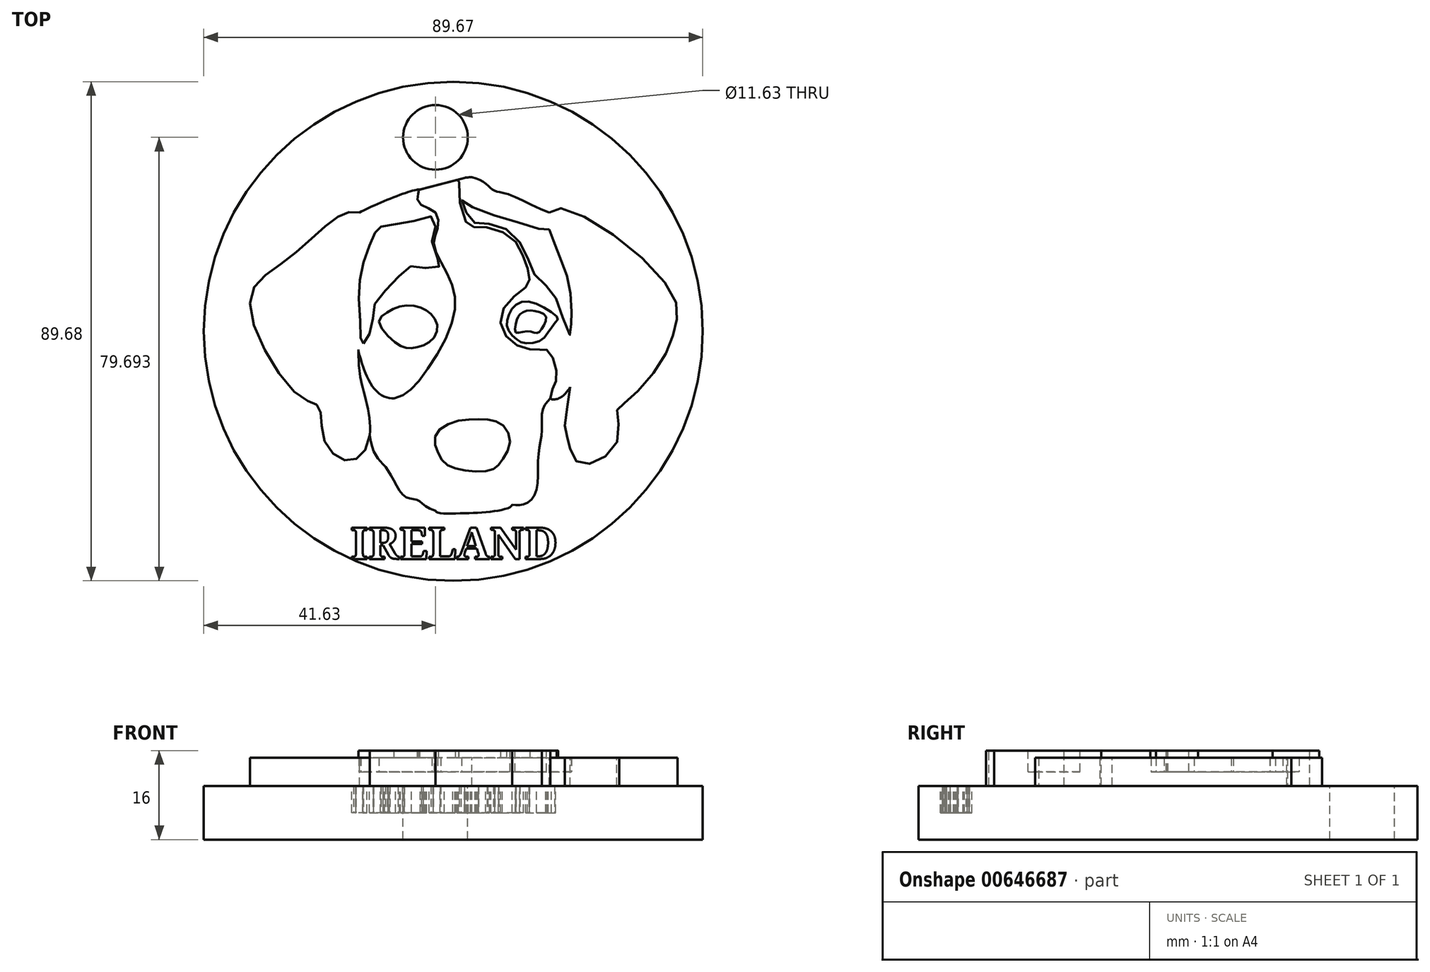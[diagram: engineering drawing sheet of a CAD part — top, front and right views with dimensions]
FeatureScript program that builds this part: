
annotation { "Feature Type Name" : "Feature", "Feature Type Description" : "" }
export const myFeature = defineFeature(function(context is Context, id is Id, definition is map)
    precondition{}
    {
        {
            var Q0;
            Q0=qCreatedBy(makeId("Top.planeOp"),FACE);
            var sketch = newSketch(context, id + "F0", { "sketchPlane" : qUnion([Q0])});
            skFitSpline(sketch, "E0", {"points": [v(-13.66, 27.6) * mm, v(-17.78, 26.67) * mm, v(-26.99, 18.92) * mm, v(-33.34, 11.59) * mm, v(-24.19, -5.58) * mm, v(-20.88, -7.44) * mm, v(-19.85, -13.65) * mm, v(-15.1, -16.96) * mm, v(-11.8, -12.41) * mm, v(-13.44, -2.27) * mm, v(-13.85, 2.98) * mm, v(-13.45, 18.91) * mm, v(-11.04, 25.53) * mm, v(-13.66, 27.6) * mm]});
            skFitSpline(sketch, "E1", {"points": [v(0, -25.98) * mm, v(3.57, -26.47) * mm, v(11.16, -25.98) * mm, v(13.75, -24.88) * mm, v(10.75, -22.95) * mm, v(6.62, -21.3) * mm, v(3.93, -22.74) * mm, v(0, -25.98) * mm]});
            skFitSpline(sketch, "E2", {"points": [v(23.24, -10.9) * mm, v(24.17, -3.78) * mm, v(23.78, 0) * mm, v(25.02, 13.65) * mm, v(20.47, 27.6) * mm, v(26.06, 27.2) * mm, v(42.53, 13.13) * mm, v(43.15, 7.35) * mm, v(40.44, 0.6) * mm, v(34.11, -6.54) * mm, v(32.64, -7.95) * mm, v(32.88, -12.87) * mm, v(28.45, -17.37) * mm, v(25.02, -16.8) * mm, v(23.78, -13.02) * mm, v(23.24, -10.9) * mm]});
            skFitSpline(sketch, "E3", {"points": [v(-13.66, 27.6) * mm, v(-2.96, 31.69) * mm, v(-3.17, 30.85) * mm, v(-2.86, 29.23) * mm, v(0, 27.6) * mm, v(0.34, 24.56) * mm, v(-0.27, 21.79) * mm, v(2.5, 15.8) * mm, v(3.07, 8.14) * mm, v(-3.5, -3.23) * mm, v(-7.45, -5.77) * mm], "startDerivative": vector(49.88, 27.02) * mm, "endDerivative": vector(-51.5, -11.1) * mm});
            skFitSpline(sketch, "E4", {"points": [v(-7.45, -5.77) * mm, v(-10.9, -4.19) * mm, v(-13.44, 1.24) * mm, v(-13.85, 2.98) * mm], "startDerivative": vector(-9.26, -1.19) * mm, "endDerivative": vector(-0.89, 6.86) * mm});
            skFitSpline(sketch, "E5", {"points": [v(6.53, 33.93) * mm, v(4.34, 33.05) * mm, v(5.76, 25.5) * mm, v(7.62, 25.06) * mm, v(13.32, 23.41) * mm, v(16.05, 19.03) * mm, v(16.93, 15.64) * mm, v(16.08, 14.05) * mm, v(12.22, 10.38) * mm, v(12.4, 5.78) * mm, v(16.08, 3.19) * mm, v(18.66, 2.98) * mm, v(19.89, 2.98) * mm, v(21.2, 1.24) * mm, v(21.75, -2.27) * mm, v(21.2, -3.75) * mm, v(20.65, -5.77) * mm, v(22.19, -5.77) * mm, v(24.17, -3.78) * mm], "startDerivative": vector(-56.64, 0.9) * mm, "endDerivative": vector(31.08, 53.1) * mm});
            skFitSpline(sketch, "E6", {"points": [v(6.53, 33.93) * mm, v(10.37, 31.69) * mm, v(13.2, 30.85) * mm, v(20.47, 27.6) * mm], "startDerivative": vector(20.86, -3.29) * mm, "endDerivative": vector(18.77, -6.28) * mm});
            skLineSegment(sketch, "E7", {"start": v(-2.96, 31.69) * mm, "end": v(5.26, 33.84) * mm});
            skFitSpline(sketch, "E8", {"points": [v(0, -25.98) * mm, v(-3.11, -24.12) * mm, v(-5.41, -23.46) * mm, v(-8.37, -18.97) * mm, v(-10.34, -16.56) * mm, v(-11.8, -12.41) * mm], "startDerivative": vector(-27.57, 6.34) * mm, "endDerivative": vector(-3.27, 28.64) * mm});
            skFitSpline(sketch, "E9", {"points": [v(13.75, -24.88) * mm, v(15.73, -24.88) * mm, v(17.92, -22.95) * mm, v(18.46, -16.45) * mm, v(19.12, -11.63) * mm, v(19.23, -8.02) * mm, v(20.65, -5.77) * mm], "startDerivative": vector(15.52, -2.17) * mm, "endDerivative": vector(13.18, 11.7) * mm});
            skFitSpline(sketch, "E10", {"points": [v(2.15, -17.77) * mm, v(0.52, -15.73) * mm, v(0, -12.4) * mm, v(3.62, -9.95) * mm, v(8.39, -9.56) * mm, v(11.64, -10.26) * mm, v(13.43, -13.39) * mm, v(11.9, -17) * mm, v(10.36, -18.53) * mm, v(6.3, -18.86) * mm, v(2.15, -17.77) * mm]});
            skFitSpline(sketch, "E11", {"points": [v(-8.57, 8.24) * mm, v(-7.53, 9.28) * mm, v(-5.74, 9.76) * mm, v(-4.01, 9.42) * mm, v(-2.9, 8.1) * mm, v(-2.84, 6.1) * mm, v(-4.01, 5.55) * mm, v(-6.08, 5.62) * mm, v(-7.8, 7.14) * mm, v(-8.57, 8.24) * mm]});
            skFitSpline(sketch, "E12", {"points": [v(14.44, 6.05) * mm, v(15.87, 6.21) * mm, v(17.51, 6.1) * mm, v(18.4, 6) * mm, v(19.16, 6.81) * mm, v(19.89, 8.84) * mm, v(18.4, 9.77) * mm, v(16.36, 9.94) * mm, v(15.05, 9.17) * mm, v(14.55, 7.96) * mm, v(14.44, 6.05) * mm]});
            skFitSpline(sketch, "E13", {"points": [v(-10.13, 8) * mm, v(-8.57, 9.74) * mm, v(-5.74, 10.87) * mm, v(-2.65, 10.52) * mm, v(-0.74, 9.28) * mm, v(0.36, 7.1) * mm, v(-0.75, 4.59) * mm, v(-3.14, 3.45) * mm, v(-5.08, 3.25) * mm, v(-7.25, 4.3) * mm, v(-10.13, 8) * mm]});
            skFitSpline(sketch, "E14", {"points": [v(12.9, 8.26) * mm, v(13.84, 10.38) * mm, v(15.89, 11.62) * mm, v(19.75, 10.38) * mm, v(22, 8.58) * mm, v(21.8, 8.13) * mm, v(20.4, 6.28) * mm, v(18.89, 4.6) * mm, v(16.14, 4.1) * mm, v(14.57, 4.8) * mm, v(13.1, 6.53) * mm, v(12.9, 8.26) * mm]});
            skFitSpline(sketch, "E15", {"points": [v(-12.92, 4.07) * mm, v(-12, 5.37) * mm, v(-11.2, 8.75) * mm, v(-10.7, 11.58) * mm, v(-7.39, 15.2) * mm, v(-4.56, 17.91) * mm, v(-1.6, 17.6) * mm, v(0.8, 17.98) * mm, v(0.93, 18.31) * mm, v(-0.57, 21.79) * mm, v(0, 24.99) * mm, v(-0.57, 26.82) * mm, v(-4.74, 25.84) * mm, v(-8.78, 25.33) * mm, v(-10.6, 24.56) * mm, v(-10.86, 23.85) * mm, v(-12.26, 20.72) * mm, v(-13.43, 16.42) * mm, v(-13.73, 11.59) * mm, v(-13.43, 5.63) * mm, v(-13.43, 4.37) * mm, v(-12.92, 4.07) * mm]});
            skFitSpline(sketch, "E16", {"points": [v(5.52, 27.6) * mm, v(4.74, 29.78) * mm, v(6.5, 28.65) * mm, v(13.77, 26.16) * mm, v(19.38, 24.56) * mm, v(20.4, 24.56) * mm, v(20.95, 23.33) * mm, v(23, 17.96) * mm, v(23.92, 15.13) * mm, v(24.46, 10.05) * mm, v(24.36, 8.25) * mm, v(24.27, 5.56) * mm, v(22.66, 9.42) * mm, v(20.85, 13.52) * mm, v(18.07, 16.1) * mm, v(16.75, 19.04) * mm, v(14.2, 23.43) * mm, v(10.06, 25.53) * mm, v(7.08, 25.72) * mm, v(5.52, 27.6) * mm]});
            skSolve(sketch);
        }
        {
            var Q0;
            Q0=qSketchRegion(id+"F0",true);
            var Q1;
            Q1=makeQuery(id+"F0.imprint","IMPRINT",FACE,{"disambiguationData":[TD([[makeQuery(id+"F0.imprint","IMPRINT",EDGE,{"derivedFrom":sQuery(id+"F0.wireOp",EDGE,"E11")}),1.0]])]});
            var Q2;
            Q2=makeQuery(id+"F0.imprint","IMPRINT",FACE,{"disambiguationData":[TD([[makeQuery(id+"F0.imprint","IMPRINT",EDGE,{"derivedFrom":sQuery(id+"F0.wireOp",EDGE,"E15")}),1.0]])]});
            var Q3;
            Q3=makeQuery(id+"F0.imprint","IMPRINT",FACE,{"disambiguationData":[TD([[makeQuery(id+"F0.imprint","IMPRINT",EDGE,{"derivedFrom":sQuery(id+"F0.wireOp",EDGE,"E12")}),1.0]])]});
            var Q4;
            Q4=makeQuery(id+"F0.imprint","IMPRINT",FACE,{"disambiguationData":[TD([[makeQuery(id+"F0.imprint","IMPRINT",EDGE,{"derivedFrom":sQuery(id+"F0.wireOp",EDGE,"E12")}),-1.0]])]});
            var Q5;
            Q5=makeQuery(id+"F0.imprint","IMPRINT",FACE,{"disambiguationData":[TD([[makeQuery(id+"F0.imprint","IMPRINT",EDGE,{"derivedFrom":sQuery(id+"F0.wireOp",EDGE,"E16")}),-1.0]])]});
            var Q6;
            Q6=makeQuery(id+"F0.imprint","IMPRINT",FACE,{"disambiguationData":[TD([[makeQuery(id+"F0.imprint","IMPRINT",EDGE,{"derivedFrom":sQuery(id+"F0.wireOp",EDGE,"E11")}),-1.0]])]});
            var Q7;
            Q7=makeQuery(id+"F0.imprint","IMPRINT",FACE,{"disambiguationData":[TD([[makeQuery(id+"F0.imprint","IMPRINT",EDGE,{"derivedFrom":sQuery(id+"F0.wireOp",EDGE,"E10")}),-1.0]])]});
            extrude(context, id + "F1", {"entities" : qUnion([Q0, Q1, Q2, Q3, Q4, Q5, Q6, Q7]), "oppositeDirection" : true, "depth" : 6.35 * mm});
        }
        {
            var Q0;
            {var subQ0=sQuery(id+"F0.wireOp",EDGE,"E0");var subQ1=makeQuery(id+"F0.imprint","INTERSECT",VERTEX,{"derivedFrom":[subQ0,sQuery(id+"F0.wireOp",EDGE,"E3")]});Q0=makeQuery(id+"F0.imprint","IMPRINT",FACE,{"disambiguationData":[TD([[makeQuery(id+"F0.imprint","IMPRINT",EDGE,{"disambiguationData":[TD([[subQ1,-1.0]])],"derivedFrom":subQ0}),1.0]])]});}
            var Q1;
            {var subQ0=sQuery(id+"F0.wireOp",EDGE,"E4");Q1=makeQuery(id+"F0.imprint","IMPRINT",FACE,{"disambiguationData":[TD([[makeQuery(id+"F0.imprint","IMPRINT",EDGE,{"derivedFrom":subQ0}),-1.0]])]});}
            var Q2;
            {var subQ5=sQuery(id+"F0.wireOp",EDGE,"E6");Q2=makeQuery(id+"F0.imprint","IMPRINT",FACE,{"disambiguationData":[TD([[makeQuery(id+"F0.imprint","IMPRINT",EDGE,{"derivedFrom":subQ5}),-1.0]])]});}
            var Q3;
            {var subQ0=sQuery(id+"F0.wireOp",EDGE,"E2");var subQ1=makeQuery(id+"F0.imprint","INTERSECT",VERTEX,{"derivedFrom":[subQ0,sQuery(id+"F0.wireOp",EDGE,"E5")]});Q3=makeQuery(id+"F0.imprint","IMPRINT",FACE,{"disambiguationData":[TD([[makeQuery(id+"F0.imprint","IMPRINT",EDGE,{"disambiguationData":[TD([[subQ1,-1.0]])],"derivedFrom":subQ0}),-1.0]])]});}
            extrude(context, id + "F2", {"entities" : qUnion([Q0, Q1, Q2, Q3]), "operationType" : NewBodyOperationType.REMOVE, "oppositeDirection" : true, "depth" : 1.27 * mm});
        }
        {
            var Q0;
            Q0=makeQuery(id+"F0.imprint","IMPRINT",FACE,{"disambiguationData":[TD([[makeQuery(id+"F0.imprint","IMPRINT",EDGE,{"derivedFrom":sQuery(id+"F0.wireOp",EDGE,"E15")}),1.0]])]});
            var Q1;
            Q1=makeQuery(id+"F0.imprint","IMPRINT",FACE,{"disambiguationData":[TD([[makeQuery(id+"F0.imprint","IMPRINT",EDGE,{"derivedFrom":sQuery(id+"F0.wireOp",EDGE,"E11")}),-1.0]])]});
            var Q2;
            Q2=makeQuery(id+"F0.imprint","IMPRINT",FACE,{"disambiguationData":[TD([[makeQuery(id+"F0.imprint","IMPRINT",EDGE,{"derivedFrom":sQuery(id+"F0.wireOp",EDGE,"E11")}),1.0]])]});
            var Q3;
            Q3=makeQuery(id+"F0.imprint","IMPRINT",FACE,{"disambiguationData":[TD([[makeQuery(id+"F0.imprint","IMPRINT",EDGE,{"derivedFrom":sQuery(id+"F0.wireOp",EDGE,"E16")}),-1.0]])]});
            var Q4;
            Q4=makeQuery(id+"F0.imprint","IMPRINT",FACE,{"disambiguationData":[TD([[makeQuery(id+"F0.imprint","IMPRINT",EDGE,{"derivedFrom":sQuery(id+"F0.wireOp",EDGE,"E12")}),1.0]])]});
            var Q5;
            Q5=makeQuery(id+"F0.imprint","IMPRINT",FACE,{"disambiguationData":[TD([[makeQuery(id+"F0.imprint","IMPRINT",EDGE,{"derivedFrom":sQuery(id+"F0.wireOp",EDGE,"E10")}),-1.0]])]});
            extrude(context, id + "F3", {"entities" : qUnion([Q0, Q1, Q2, Q3, Q4, Q5]), "operationType" : NewBodyOperationType.REMOVE, "oppositeDirection" : true, "depth" : 3.8 * mm});
        }
        {
            var Q0;
            {var subQ0=sQuery(id+"F0.wireOp",EDGE,"E7");var subQ1=sQuery(id+"F0.wireOp",EDGE,"E5");Q0=makeQuery(id+"F2.boolean.opBoolean","SPLIT",EDGE,{"disambiguationData":[topologyDisambiguationEdgeConnected([makeQuery(id+"F2.opExtrude","SWEPT_FACE",FACE,{"disambiguationData":[OSD([subQ1])]})])],"derivedFrom":makeQuery(id+"F1.opExtrude","SWEPT_EDGE",EDGE,{"disambiguationData":[OSD([subQ1,subQ0])]})});}
            var Q1;
            {var subQ0=sQuery(id+"F0.wireOp",EDGE,"E7");var subQ1=sQuery(id+"F0.wireOp",EDGE,"E3");Q1=makeQuery(id+"F2.boolean.opBoolean","SPLIT",EDGE,{"disambiguationData":[topologyDisambiguationEdgeConnected([makeQuery(id+"F2.opExtrude","SWEPT_FACE",FACE,{"disambiguationData":[OSD([subQ1])]})])],"derivedFrom":makeQuery(id+"F1.opExtrude","SWEPT_EDGE",EDGE,{"disambiguationData":[OSD([subQ1,subQ0])]})});}
            fillet(context, id + "F4", {"entities" : qUnion([Q0, Q1]), "radius" : 0.5 * mm, "tangentPropagation" : true, "allowEdgeOverflow" : false});
        }
        {
            var Q0;
            Q0=makeQuery(id+"F1.opExtrude","CAP_FACE",FACE,{"disambiguationData":[OSD([sQuery(id+"F0.wireOp",EDGE,"E0"),sQuery(id+"F0.wireOp",EDGE,"E1"),sQuery(id+"F0.wireOp",EDGE,"E2"),sQuery(id+"F0.wireOp",EDGE,"E3"),sQuery(id+"F0.wireOp",EDGE,"E5"),sQuery(id+"F0.wireOp",EDGE,"E6"),sQuery(id+"F0.wireOp",EDGE,"E7"),sQuery(id+"F0.wireOp",EDGE,"E8"),sQuery(id+"F0.wireOp",EDGE,"E9")])],"isStart":false});
            var sketch = newSketch(context, id + "F5", { "sketchPlane" : qUnion([Q0])});
            skCircle(sketch, "E17", {"center": v(3.2, -6.26) * mm, "radius": 44.84 * mm});
            skSolve(sketch);
        }
        {
            var Q0;
            Q0 = qSketchRegion(id + "F5", true);
            extrude(context, id + "F6", {"entities" : qUnion([Q0]), "operationType" : NewBodyOperationType.ADD, "depth" : 9.65 * mm, "offsetDistance" : 25.4 * mm});
        }
        {
            var Q0;
            Q0=makeQuery(id+"F6.opExtrude","CAP_FACE",FACE,{"disambiguationData":[OSD([sQuery(id+"F5.wireOp",EDGE,"E17")])],"isStart":true});
            var sketch = newSketch(context, id + "F7", { "sketchPlane" : qUnion([Q0])});
            skCircle(sketch, "E18", {"center": v(0, 41.11) * mm, "radius": 5.81 * mm});
            skSolve(sketch);
        }
        {
            var Q0;
            Q0 = qSketchRegion(id + "F7", true);
            extrude(context, id + "F8", {"entities" : qUnion([Q0]), "operationType" : NewBodyOperationType.REMOVE, "oppositeDirection" : true, "depth" : 25.4 * mm, "offsetDistance" : 25.4 * mm});
        }
        {
            var Q0;
            Q0=makeQuery(id+"F6.opExtrude","CAP_FACE",FACE,{"disambiguationData":[OSD([sQuery(id+"F5.wireOp",EDGE,"E17")])],"isStart":true});
            var sketch = newSketch(context, id + "F9", { "sketchPlane" : qUnion([Q0])});
            skText(sketch, "E19", { "text": "IRELAND", "fontName": "NotoSerif-Bold.ttf"});
            const initialGuessF9  = {"E19": [-0.01525, -0.03466, 1, 0, 0.00568]};
            skSetInitialGuess(sketch, initialGuessF9);
            skSolve(sketch);
        }
        {
            var Q0;
            Q0 = qSketchRegion(id + "F9", true);
            extrude(context, id + "F10", {"entities" : qUnion([Q0]), "operationType" : NewBodyOperationType.REMOVE, "oppositeDirection" : true, "depth" : 4.83 * mm, "offsetDistance" : 25.4 * mm});
        }
    });
